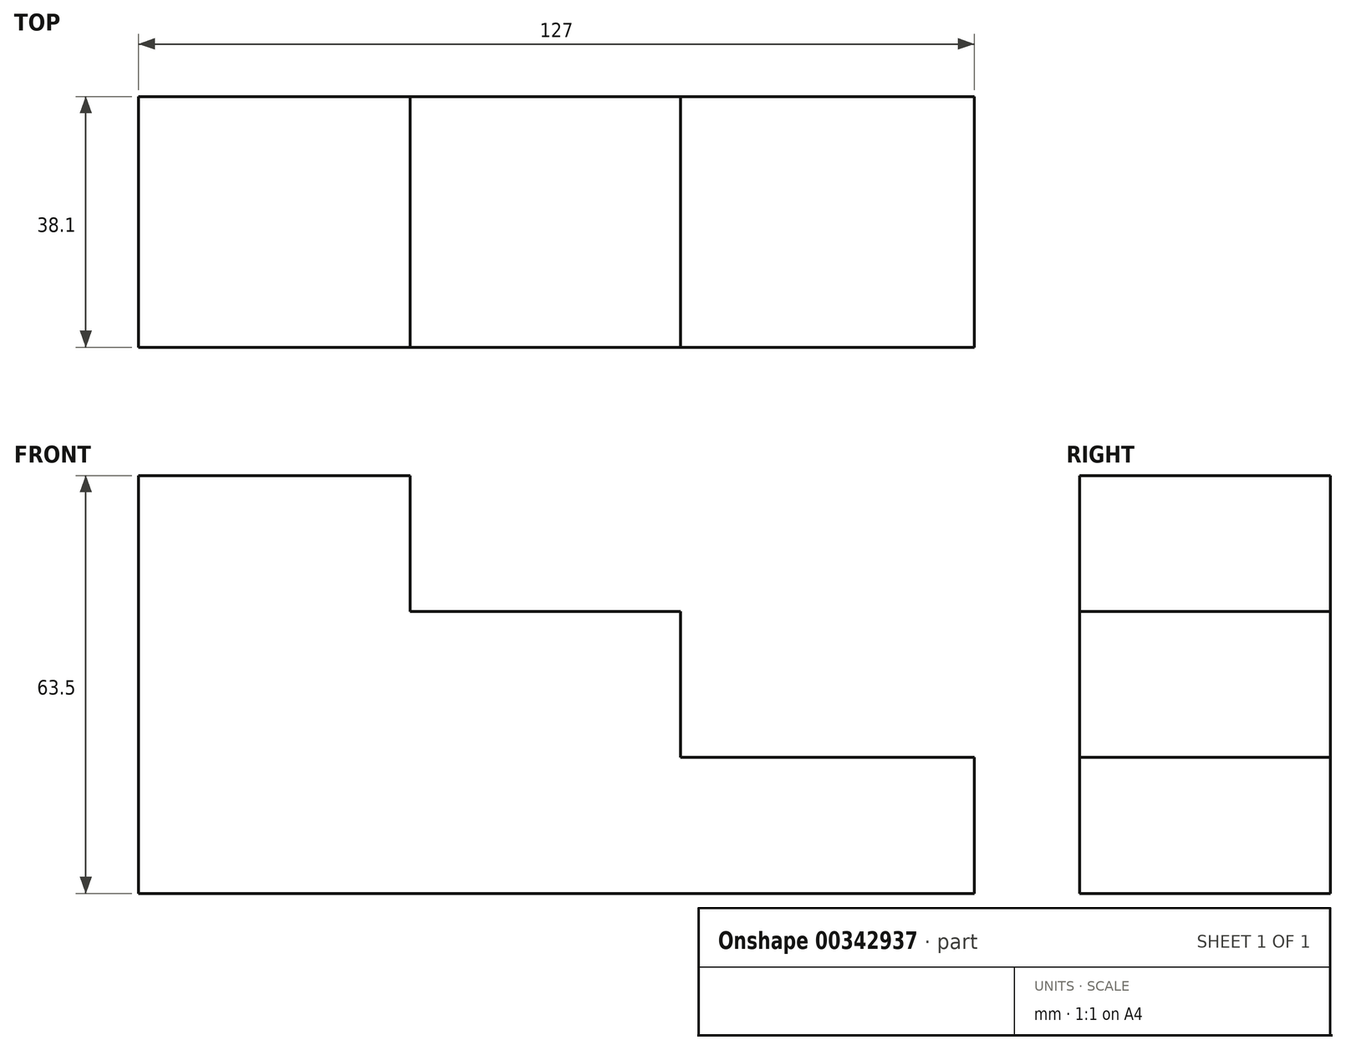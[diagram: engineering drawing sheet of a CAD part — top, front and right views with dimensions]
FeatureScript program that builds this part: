
annotation { "Feature Type Name" : "Feature", "Feature Type Description" : "" }
export const myFeature = defineFeature(function(context is Context, id is Id, definition is map)
    precondition{}
    {
        {
            var Q0;
            Q0=qCreatedBy(makeId("Front.planeOp"),FACE);
            var sketch = newSketch(context, id + "F0", { "sketchPlane" : qUnion([Q0])});
            skLineSegment(sketch, "E0", {"start": v(-69.3, 53.57) * mm, "end": v(-69.3, -9.93) * mm});
            skLineSegment(sketch, "E1", {"start": v(-69.3, -9.93) * mm, "end": v(57.7, -9.93) * mm});
            skLineSegment(sketch, "E2", {"start": v(-69.3, 53.57) * mm, "end": v(-28.03, 53.57) * mm});
            skLineSegment(sketch, "E3", {"start": v(-28.03, 53.57) * mm, "end": v(-28.03, 32.93) * mm});
            skLineSegment(sketch, "E4", {"start": v(-28.03, 32.93) * mm, "end": v(13.07, 32.93) * mm});
            skLineSegment(sketch, "E5", {"start": v(57.7, -9.93) * mm, "end": v(57.7, 10.72) * mm});
            skLineSegment(sketch, "E6", {"start": v(57.7, 10.72) * mm, "end": v(16.42, 10.72) * mm});
            skLineSegment(sketch, "E7", {"start": v(13.07, 32.93) * mm, "end": v(13.07, 10.72) * mm});
            skLineSegment(sketch, "E8", {"start": v(13.07, 10.72) * mm, "end": v(16.42, 10.72) * mm});
            skSolve(sketch);
        }
        {
            var Q0;
            Q0 = qSketchRegion(id + "F0", true);
            extrude(context, id + "F1", {"entities" : qUnion([Q0]), "depth" : 38.1 * mm});
        }
    });
